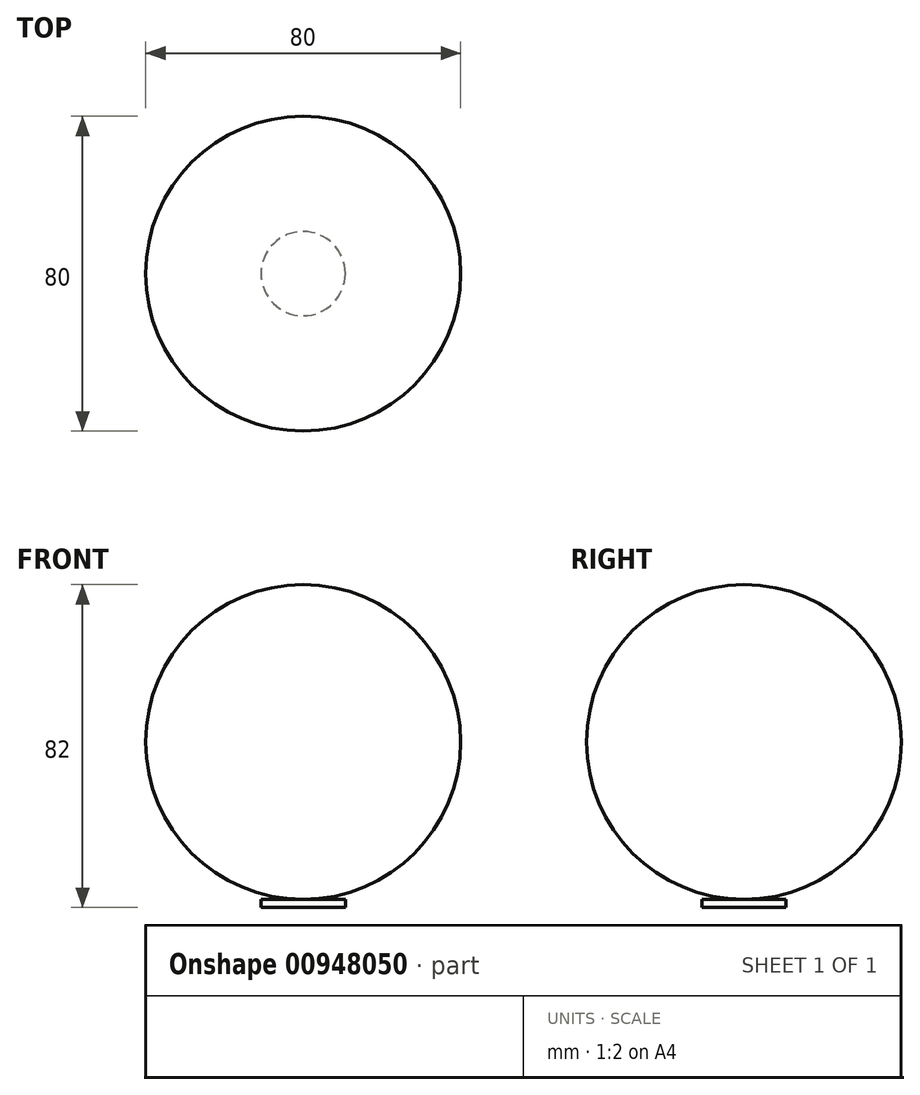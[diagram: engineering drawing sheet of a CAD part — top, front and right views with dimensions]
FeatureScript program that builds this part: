
annotation { "Feature Type Name" : "Feature", "Feature Type Description" : "" }
export const myFeature = defineFeature(function(context is Context, id is Id, definition is map)
    precondition{}
    {
        {
            var Q0;
            Q0=qCreatedBy(makeId("Top.planeOp"),FACE);
            var sketch = newSketch(context, id + "F0", { "sketchPlane" : qUnion([Q0])});
            skCircle(sketch, "E0", {"center": v(0, 0) * mm, "radius": 40 * mm});
            skSolve(sketch);
        }
        {
            var Q0;
            Q0 = qSketchRegion(id + "F0", true);
            extrude(context, id + "F1", {"entities" : qUnion([Q0]), "depth" : 80 * mm, "offsetDistance" : 25 * mm});
        }
        {
            var Q0;
            Q0=makeQuery(id+"F1.opExtrude","CAP_FACE",FACE,{"disambiguationData":[OSD([sQuery(id+"F0.wireOp",EDGE,"E0")])],"isStart":false});
            var Q1;
            Q1=makeQuery(id+"F1.opExtrude","CAP_EDGE",EDGE,{"disambiguationData":[OSD([sQuery(id+"F0.wireOp",EDGE,"E0")])],"isStart":true});
            fillet(context, id + "F2", {"entities" : qUnion([Q0, Q1]), "radius" : 40 * mm, "tangentPropagation" : true, "allowEdgeOverflow" : false});
        }
        {
            var Q0;
            Q0=qCreatedBy(makeId("Top.planeOp"),FACE);
            var sketch = newSketch(context, id + "F3", { "sketchPlane" : qUnion([Q0])});
            skCircle(sketch, "E1", {"center": v(0, 0) * mm, "radius": 10.7 * mm});
            skSolve(sketch);
        }
        {
            var Q0;
            Q0 = qSketchRegion(id + "F3", true);
            var Q1;
            Q1=makeQuery(id+"F3.imprint","IMPRINT",FACE,{"disambiguationData":[TD([[makeQuery(id+"F3.imprint","IMPRINT",EDGE,{"derivedFrom":sQuery(id+"F3.wireOp",EDGE,"E1")}),1.0]])]});
            extrude(context, id + "F4", {"entities" : qUnion([Q0, Q1]), "oppositeDirection" : true, "depth" : 2 * mm, "offsetDistance" : 25 * mm});
        }
    });
